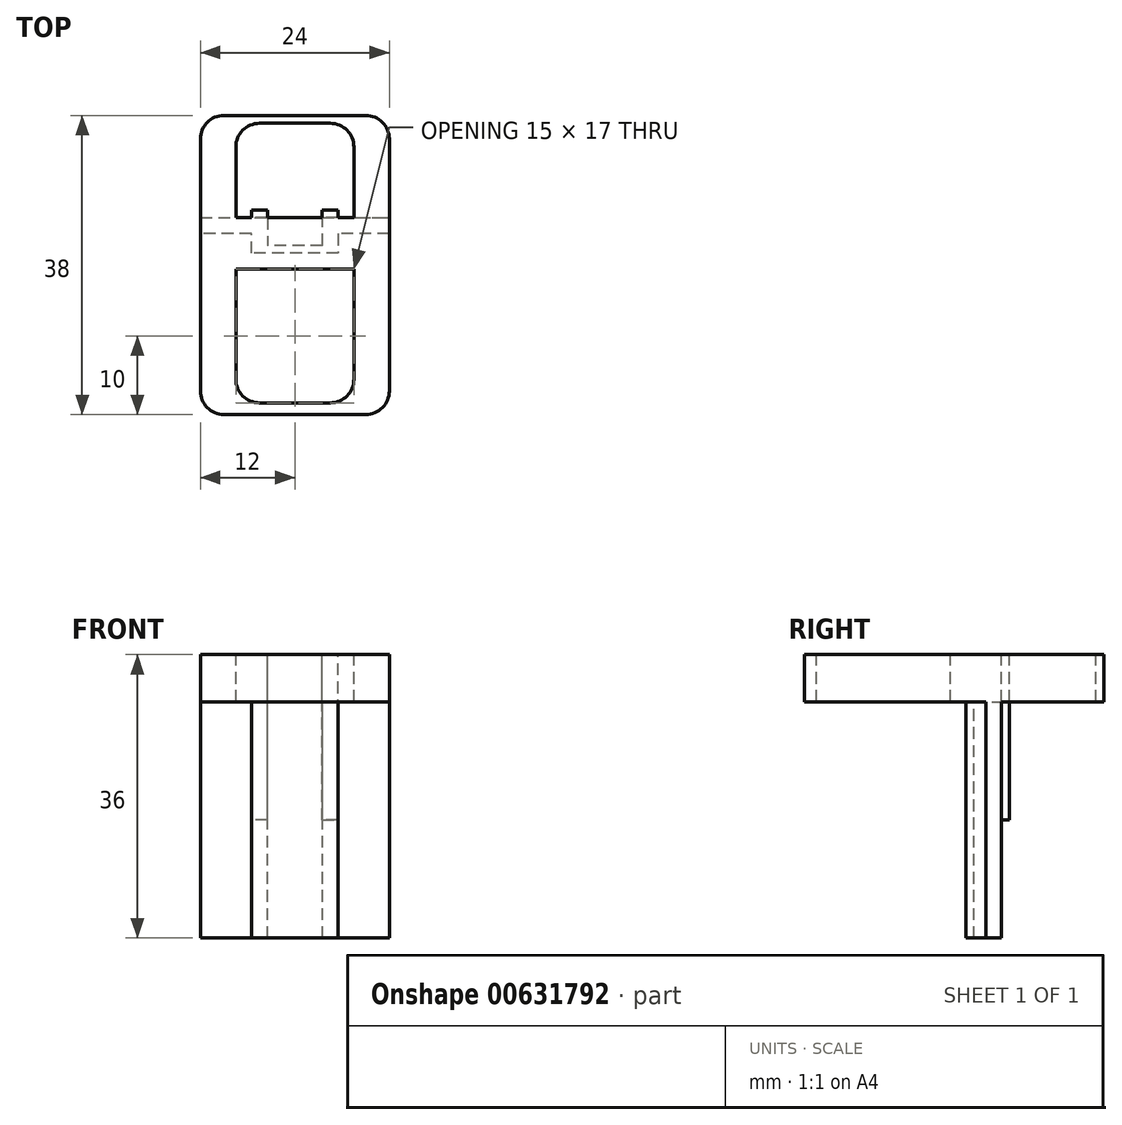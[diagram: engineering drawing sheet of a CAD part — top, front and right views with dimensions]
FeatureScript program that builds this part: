
annotation { "Feature Type Name" : "Feature", "Feature Type Description" : "" }
export const myFeature = defineFeature(function(context is Context, id is Id, definition is map)
    precondition{}
    {
        {
            var Q0;
            Q0=qCreatedBy(makeId("Top.planeOp"),FACE);
            var sketch = newSketch(context, id + "F0", { "sketchPlane" : qUnion([Q0])});
            skLineSegment(sketch, "E0.bottom", {"start": v(9, 19) * mm, "end": v(-9, 19) * mm});
            skLineSegment(sketch, "E0.top", {"start": v(9, -19) * mm, "end": v(-9, -19) * mm});
            skLineSegment(sketch, "E0.left", {"start": v(12, 16) * mm, "end": v(12, -16) * mm});
            skLineSegment(sketch, "E0.right", {"start": v(-12, 16) * mm, "end": v(-12, -16) * mm});
            skPoint(sketch, "E0.middle", {"position": v(0, 0) * mm});
            skPoint(sketch, "E1.visualSharp", {"position": v(-12, 19) * mm});
            skArc(sketch, "E1.filletArc", {"start": v(-9, 19) * mm, "mid": v(-11.12, 18.12) * mm, "end": v(-12, 16) * mm});
            skPoint(sketch, "E2.visualSharp", {"position": v(12, 19) * mm});
            skArc(sketch, "E2.filletArc", {"start": v(12, 16) * mm, "mid": v(11.12, 18.12) * mm, "end": v(9, 19) * mm});
            skPoint(sketch, "E3.visualSharp", {"position": v(-12, -19) * mm});
            skArc(sketch, "E3.filletArc", {"start": v(-12, -16) * mm, "mid": v(-11.12, -18.12) * mm, "end": v(-9, -19) * mm});
            skPoint(sketch, "E4.visualSharp", {"position": v(12, -19) * mm});
            skArc(sketch, "E4.filletArc", {"start": v(9, -19) * mm, "mid": v(11.12, -18.12) * mm, "end": v(12, -16) * mm});
            skSolve(sketch);
        }
        {
            var Q0;
            Q0=makeQuery(id+"F0.imprint","IMPRINT",FACE,{"disambiguationData":[TD([[makeQuery(id+"F0.imprint","IMPRINT",EDGE,{"derivedFrom":sQuery(id+"F0.wireOp",EDGE,"E0.bottom")}),1.0]])]});
            extrude(context, id + "F1", {"entities" : qUnion([Q0]), "oppositeDirection" : true, "depth" : 6 * mm, "offsetDistance" : 25 * mm});
        }
        {
            var Q0;
            Q0=makeQuery(id+"F1.opExtrude","CAP_FACE",FACE,{"disambiguationData":[OSD([sQuery(id+"F0.wireOp",EDGE,"E0.bottom"),sQuery(id+"F0.wireOp",EDGE,"E0.top"),sQuery(id+"F0.wireOp",EDGE,"E0.left"),sQuery(id+"F0.wireOp",EDGE,"E0.right"),sQuery(id+"F0.wireOp",EDGE,"E1.filletArc"),sQuery(id+"F0.wireOp",EDGE,"E2.filletArc"),sQuery(id+"F0.wireOp",EDGE,"E3.filletArc"),sQuery(id+"F0.wireOp",EDGE,"E4.filletArc")])],"isStart":true});
            var sketch = newSketch(context, id + "F2", { "sketchPlane" : qUnion([Q0])});
            skLineSegment(sketch, "E5", {"start": v(0, 19) * mm, "end": v(0, -19) * mm, "construction": true});
            skLineSegment(sketch, "E6", {"start": v(-12, -9) * mm, "end": v(12, -9) * mm, "construction": true});
            skLineSegment(sketch, "E7", {"start": v(-12, 12) * mm, "end": v(12, 12) * mm, "construction": true});
            skLineSegment(sketch, "E8", {"start": v(12, 12) * mm, "end": v(12, 13.48) * mm});
            skPoint(sketch, "E9.middle", {"position": v(0, 12) * mm});
            skPoint(sketch, "E10.middle", {"position": v(0, -9) * mm});
            skLineSegment(sketch, "E11.bottom", {"start": v(7.5, -0.5) * mm, "end": v(-7.5, -0.5) * mm});
            skLineSegment(sketch, "E11.top", {"start": v(4.5, -17.5) * mm, "end": v(-4.5, -17.5) * mm});
            skLineSegment(sketch, "E11.left", {"start": v(7.5, -0.5) * mm, "end": v(7.5, -14.5) * mm});
            skLineSegment(sketch, "E11.right", {"start": v(-7.5, -0.5) * mm, "end": v(-7.5, -14.5) * mm});
            skLineSegment(sketch, "E12.bottom", {"start": v(4.5, 18) * mm, "end": v(-4.5, 18) * mm});
            skLineSegment(sketch, "E12.top", {"start": v(7.5, 6) * mm, "end": v(-7.5, 6) * mm});
            skLineSegment(sketch, "E12.left", {"start": v(7.5, 15) * mm, "end": v(7.5, 6) * mm});
            skLineSegment(sketch, "E12.right", {"start": v(-7.5, 15) * mm, "end": v(-7.5, 6) * mm});
            skPoint(sketch, "E13.visualSharp", {"position": v(-7.5, 18) * mm});
            skArc(sketch, "E13.filletArc", {"start": v(-4.5, 18) * mm, "mid": v(-6.62, 17.12) * mm, "end": v(-7.5, 15) * mm});
            skPoint(sketch, "E14.visualSharp", {"position": v(7.5, 18) * mm});
            skArc(sketch, "E14.filletArc", {"start": v(7.5, 15) * mm, "mid": v(6.62, 17.12) * mm, "end": v(4.5, 18) * mm});
            skPoint(sketch, "E15.visualSharp", {"position": v(-7.5, -17.5) * mm});
            skArc(sketch, "E15.filletArc", {"start": v(-7.5, -14.5) * mm, "mid": v(-6.62, -16.62) * mm, "end": v(-4.5, -17.5) * mm});
            skPoint(sketch, "E16.visualSharp", {"position": v(7.5, -17.5) * mm});
            skArc(sketch, "E16.filletArc", {"start": v(4.5, -17.5) * mm, "mid": v(6.62, -16.62) * mm, "end": v(7.5, -14.5) * mm});
            skSolve(sketch);
        }
        {
            var Q0;
            Q0=makeQuery(id+"F2.imprint","IMPRINT",FACE,{"disambiguationData":[TD([[makeQuery(id+"F2.imprint","IMPRINT",EDGE,{"derivedFrom":sQuery(id+"F2.wireOp",EDGE,"E12.bottom")}),1.0]])]});
            var Q1;
            Q1=makeQuery(id+"F2.imprint","IMPRINT",FACE,{"disambiguationData":[TD([[makeQuery(id+"F2.imprint","IMPRINT",EDGE,{"derivedFrom":sQuery(id+"F2.wireOp",EDGE,"E11.bottom")}),1.0]])]});
            extrude(context, id + "F3", {"entities" : qUnion([Q0, Q1]), "operationType" : NewBodyOperationType.REMOVE, "endBound" : BoundingType.UP_TO_NEXT, "oppositeDirection" : true, "depth" : 25 * mm, "offsetDistance" : 25 * mm});
        }
        {
            var Q0;
            Q0=makeQuery(id+"F1.opExtrude","CAP_FACE",FACE,{"disambiguationData":[OSD([sQuery(id+"F0.wireOp",EDGE,"E0.bottom"),sQuery(id+"F0.wireOp",EDGE,"E0.top"),sQuery(id+"F0.wireOp",EDGE,"E0.left"),sQuery(id+"F0.wireOp",EDGE,"E0.right"),sQuery(id+"F0.wireOp",EDGE,"E1.filletArc"),sQuery(id+"F0.wireOp",EDGE,"E2.filletArc"),sQuery(id+"F0.wireOp",EDGE,"E3.filletArc"),sQuery(id+"F0.wireOp",EDGE,"E4.filletArc")])],"isStart":false});
            var sketch = newSketch(context, id + "F4", { "sketchPlane" : qUnion([Q0])});
            skLineSegment(sketch, "E17", {"start": v(-12, -6) * mm, "end": v(12, -6) * mm, "construction": true});
            skLineSegment(sketch, "E18", {"start": v(-12, -4) * mm, "end": v(12, -4) * mm, "construction": true});
            skLineSegment(sketch, "E19.bottom", {"start": v(3.5, -2.5) * mm, "end": v(-3.5, -2.5) * mm});
            skLineSegment(sketch, "E19.top", {"start": v(3.5, -9.5) * mm, "end": v(-3.5, -9.5) * mm, "construction": true});
            skLineSegment(sketch, "E19.left", {"start": v(3.5, -2.5) * mm, "end": v(3.5, -9.5) * mm, "construction": true});
            skLineSegment(sketch, "E19.right", {"start": v(-3.5, -2.5) * mm, "end": v(-3.5, -9.5) * mm, "construction": true});
            skPoint(sketch, "E19.middle", {"position": v(0, -6) * mm});
            skLineSegment(sketch, "E20", {"start": v(-12, -2) * mm, "end": v(12, -2) * mm, "construction": true});
            skLineSegment(sketch, "E21.bottom", {"start": v(5.5, -1.5) * mm, "end": v(-5.5, -1.5) * mm});
            skLineSegment(sketch, "E21.top", {"start": v(5.5, -10.5) * mm, "end": v(-5.5, -10.5) * mm, "construction": true});
            skLineSegment(sketch, "E21.left", {"start": v(5.5, -1.5) * mm, "end": v(5.5, -10.5) * mm, "construction": true});
            skLineSegment(sketch, "E21.right", {"start": v(-5.5, -1.5) * mm, "end": v(-5.5, -10.5) * mm, "construction": true});
            skLineSegment(sketch, "E22", {"start": v(-12, -6) * mm, "end": v(-3.5, -6) * mm});
            skLineSegment(sketch, "E23", {"start": v(-3.5, -6) * mm, "end": v(-3.5, -2.5) * mm});
            skLineSegment(sketch, "E24", {"start": v(3.5, -2.5) * mm, "end": v(3.5, -6) * mm});
            skLineSegment(sketch, "E25", {"start": v(3.5, -6) * mm, "end": v(12, -6) * mm});
            skLineSegment(sketch, "E26", {"start": v(12, -4) * mm, "end": v(5.5, -4) * mm});
            skLineSegment(sketch, "E27", {"start": v(5.5, -4) * mm, "end": v(5.5, -1.5) * mm});
            skLineSegment(sketch, "E28", {"start": v(-5.5, -1.5) * mm, "end": v(-5.5, -4) * mm});
            skLineSegment(sketch, "E29", {"start": v(-5.5, -4) * mm, "end": v(-12, -4) * mm});
            skSolve(sketch);
        }
        {
            var Q0;
            Q0=makeQuery(id+"F4.imprint","IMPRINT",FACE,{"disambiguationData":[TD([[makeQuery(id+"F4.imprint","IMPRINT",EDGE,{"derivedFrom":sQuery(id+"F4.wireOp",EDGE,"E21.bottom")}),1.0]])]});
            extrude(context, id + "F5", {"entities" : qUnion([Q0]), "operationType" : NewBodyOperationType.ADD, "depth" : 30 * mm, "offsetDistance" : 25 * mm});
        }
        {
            var Q0;
            Q0=makeQuery(id+"F1.opExtrude","CAP_FACE",FACE,{"disambiguationData":[OSD([sQuery(id+"F0.wireOp",EDGE,"E0.bottom"),sQuery(id+"F0.wireOp",EDGE,"E0.top"),sQuery(id+"F0.wireOp",EDGE,"E0.left"),sQuery(id+"F0.wireOp",EDGE,"E0.right"),sQuery(id+"F0.wireOp",EDGE,"E1.filletArc"),sQuery(id+"F0.wireOp",EDGE,"E2.filletArc"),sQuery(id+"F0.wireOp",EDGE,"E3.filletArc"),sQuery(id+"F0.wireOp",EDGE,"E4.filletArc")])],"isStart":true});
            var sketch = newSketch(context, id + "F6", { "sketchPlane" : qUnion([Q0])});
            skLineSegment(sketch, "E30.bottom", {"start": v(-3.5, 6) * mm, "end": v(-5.5, 6) * mm});
            skLineSegment(sketch, "E30.top", {"start": v(-3.5, 7) * mm, "end": v(-5.5, 7) * mm});
            skLineSegment(sketch, "E30.left", {"start": v(-3.5, 6) * mm, "end": v(-3.5, 7) * mm});
            skLineSegment(sketch, "E30.right", {"start": v(-5.5, 6) * mm, "end": v(-5.5, 7) * mm});
            skLineSegment(sketch, "E31.bottom", {"start": v(3.47, 6) * mm, "end": v(5.47, 6) * mm});
            skLineSegment(sketch, "E31.top", {"start": v(3.47, 7) * mm, "end": v(5.47, 7) * mm});
            skLineSegment(sketch, "E31.left", {"start": v(3.47, 6) * mm, "end": v(3.47, 7) * mm});
            skLineSegment(sketch, "E31.right", {"start": v(5.47, 6) * mm, "end": v(5.47, 7) * mm});
            skSolve(sketch);
        }
        {
            var Q0;
            Q0=makeQuery(id+"F6.imprint","IMPRINT",FACE,{"disambiguationData":[TD([[makeQuery(id+"F6.imprint","IMPRINT",EDGE,{"derivedFrom":sQuery(id+"F6.wireOp",EDGE,"E30.bottom")}),-1.0]])]});
            var Q1;
            Q1=makeQuery(id+"F6.imprint","IMPRINT",FACE,{"disambiguationData":[TD([[makeQuery(id+"F6.imprint","IMPRINT",EDGE,{"derivedFrom":sQuery(id+"F6.wireOp",EDGE,"E31.bottom")}),-1.0]])]});
            extrude(context, id + "F7", {"entities" : qUnion([Q0, Q1]), "operationType" : NewBodyOperationType.ADD, "oppositeDirection" : true, "depth" : 21 * mm, "offsetDistance" : 25 * mm});
        }
    });
